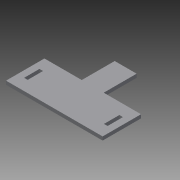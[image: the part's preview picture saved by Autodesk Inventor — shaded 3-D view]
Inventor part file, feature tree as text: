
AUTODESK INVENTOR PART (.ipt)
format: ipt  version: 2013 (Build 170138000, 138)  size: 129,024 bytes
history: native  units: mm
features: other x3, extrude x1, sketch x1
ambient origin geometry x8: Origin, YZ Plane, XZ Plane, XY Plane, X Axis, Y Axis, Z Axis, Center Point
feature tree (5):
  other  "Blocks"
  extrude  "Extrusion5"  Depth=100.0mm
  sketch  "Sketch1"  dims[d0=100.0mm d2=100.0mm d3=3.0mm d5=3.0mm d7=3.25mm d8=14.0mm d9=30.0mm d10=40.0mm d11=10.0mm d12=10.0mm d15=3.25mm d16=8.0mm d17=0.0mm d22=22.5mm d23=12.4mm d24=4.5mm d25=4.5mm d26=2.0mm d27=2.0mm d28=22.5mm d29=3.25mm d30=14.0mm d31=12.0mm d34=6.0mm d35=6.0mm d38=20.0mm d39=30.0mm d40=3.25mm d41=0.0mm d42=35.0mm d43=9.5mm d44=20.0mm]
  other  "Block1"
  other  "Block1:1"
